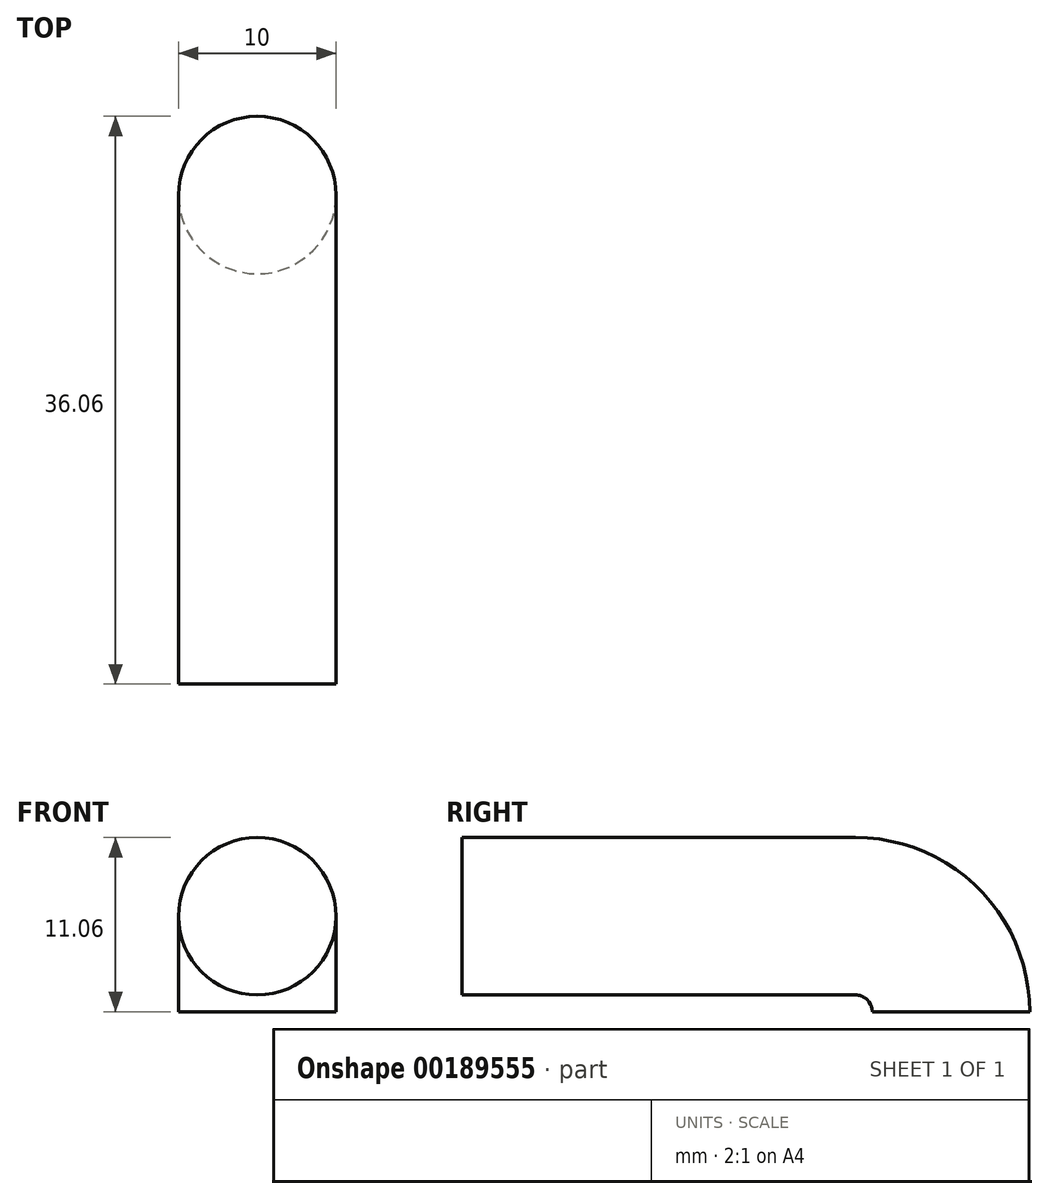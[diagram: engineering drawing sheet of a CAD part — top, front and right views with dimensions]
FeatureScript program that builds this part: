
annotation { "Feature Type Name" : "Feature", "Feature Type Description" : "" }
export const myFeature = defineFeature(function(context is Context, id is Id, definition is map)
    precondition{}
    {
        {
            var Q0;
            Q0=qCreatedBy(makeId("Top.planeOp"),FACE);
            var sketch = newSketch(context, id + "F0", { "sketchPlane" : qUnion([Q0])});
            skCircle(sketch, "E0", {"center": v(0, 0) * mm, "radius": 5 * mm});
            skSolve(sketch);
        }
        {
            var Q0;
            Q0=qCreatedBy(makeId("Top.planeOp"),FACE);
            var sketch = newSketch(context, id + "F1", { "sketchPlane" : qUnion([Q0])});
            skLineSegment(sketch, "E1", {"start": v(-9.38, -6.06) * mm, "end": v(9.23, -6.06) * mm});
            skLineSegment(sketch, "E2", {"start": v(0, -5.06) * mm, "end": v(0, -6.06) * mm});
            skSolve(sketch);
        }
        {
            var Q0;
            Q0=makeQuery(id+"F0.imprint","IMPRINT",FACE,{"disambiguationData":[TD([[makeQuery(id+"F0.imprint","IMPRINT",EDGE,{"derivedFrom":sQuery(id+"F0.wireOp",EDGE,"E0")}),1.0]])]});
            var Q1;
            Q1=sQuery(id+"F1.wireOp",EDGE,"E1");
            revolve(context, id + "F2", {"entities" : qUnion([Q0]), "axis" : qUnion([Q1]), "revolveType" : RevolveType.ONE_DIRECTION, "angle" : 90 * degree});
        }
        {
            var Q0;
            Q0=qCreatedBy(makeId("Front.planeOp"),FACE);
            var sketch = newSketch(context, id + "F3", { "sketchPlane" : qUnion([Q0])});
            skSolve(sketch);
        }
        {
            var Q0;
            Q0=qSketchRegion(id+"F3",true);
            var Q1;
            Q1=makeQuery(id+"F2.opRevolve","CAP_FACE",FACE,{"disambiguationData":[OSD([sQuery(id+"F0.wireOp",EDGE,"E0")])],"isStart":false});
            extrude(context, id + "F4", {"entities" : qUnion([Q0, Q1]), "operationType" : NewBodyOperationType.ADD, "depth" : 25 * mm});
        }
    });
